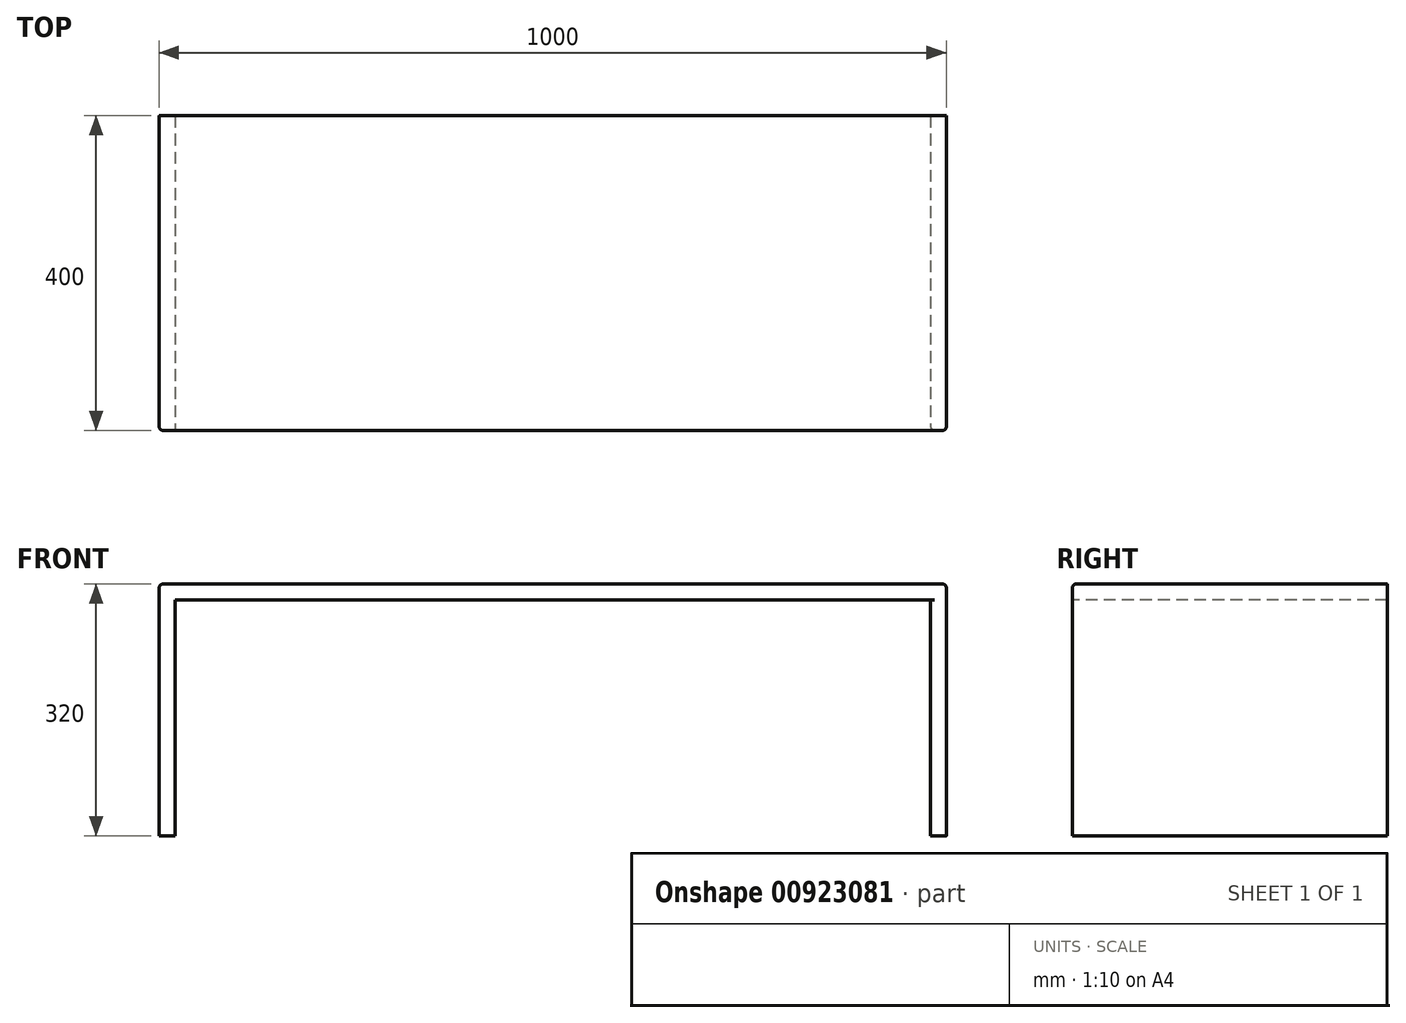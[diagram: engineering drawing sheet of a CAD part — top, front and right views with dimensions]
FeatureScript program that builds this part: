
annotation { "Feature Type Name" : "Feature", "Feature Type Description" : "" }
export const myFeature = defineFeature(function(context is Context, id is Id, definition is map)
    precondition{}
    {
        {
            var Q0;
            Q0=qCreatedBy(makeId("Top.planeOp"),FACE);
            var sketch = newSketch(context, id + "F0", { "sketchPlane" : qUnion([Q0])});
            skLineSegment(sketch, "E0.bottom", {"start": v(-578.88, 126.54) * mm, "end": v(421.12, 126.54) * mm});
            skLineSegment(sketch, "E0.top", {"start": v(-578.88, -273.46) * mm, "end": v(421.12, -273.46) * mm});
            skLineSegment(sketch, "E0.left", {"start": v(-578.88, 126.54) * mm, "end": v(-578.88, -273.46) * mm});
            skLineSegment(sketch, "E0.right", {"start": v(421.12, 126.54) * mm, "end": v(421.12, -273.46) * mm});
            skSolve(sketch);
        }
        {
            var Q0;
            Q0=makeQuery(id+"F0.imprint","IMPRINT",FACE,{"disambiguationData":[TD([[makeQuery(id+"F0.imprint","IMPRINT",EDGE,{"derivedFrom":sQuery(id+"F0.wireOp",EDGE,"E0.bottom")}),-1.0]])]});
            extrude(context, id + "F1", {"entities" : qUnion([Q0]), "depth" : 20 * mm, "offsetDistance" : 25 * mm});
        }
        {
            var Q0;
            Q0=makeQuery(id+"F0.imprint","IMPRINT",FACE,{"disambiguationData":[TD([[makeQuery(id+"F0.imprint","IMPRINT",EDGE,{"derivedFrom":sQuery(id+"F0.wireOp",EDGE,"E0.bottom")}),-1.0]])]});
            var sketch = newSketch(context, id + "F2", { "sketchPlane" : qUnion([Q0])});
            skLineSegment(sketch, "E1.bottom", {"start": v(-578.88, 126.54) * mm, "end": v(-558.88, 126.54) * mm});
            skLineSegment(sketch, "E1.top", {"start": v(-578.88, -273.46) * mm, "end": v(-558.88, -273.46) * mm});
            skLineSegment(sketch, "E1.left", {"start": v(-578.88, 126.54) * mm, "end": v(-578.88, -273.46) * mm});
            skLineSegment(sketch, "E1.right", {"start": v(-558.88, 126.54) * mm, "end": v(-558.88, -273.46) * mm});
            skLineSegment(sketch, "E2.bottom", {"start": v(421.12, 126.54) * mm, "end": v(401.12, 126.54) * mm});
            skLineSegment(sketch, "E2.top", {"start": v(421.12, -273.46) * mm, "end": v(401.12, -273.46) * mm});
            skLineSegment(sketch, "E2.left", {"start": v(421.12, 126.54) * mm, "end": v(421.12, -273.46) * mm});
            skLineSegment(sketch, "E2.right", {"start": v(401.12, 126.54) * mm, "end": v(401.12, -273.46) * mm});
            skSolve(sketch);
        }
        {
            var Q0;
            Q0 = qSketchRegion(id + "F2", true);
            extrude(context, id + "F3", {"entities" : qUnion([Q0]), "operationType" : NewBodyOperationType.ADD, "oppositeDirection" : true, "depth" : 300 * mm, "offsetDistance" : 25 * mm});
        }
        {
            var Q0;
            Q0=makeQuery(id+"F1.opExtrude","CAP_EDGE",EDGE,{"disambiguationData":[OSD([sQuery(id+"F0.wireOp",EDGE,"E0.top")])],"isStart":false});
            fillet(context, id + "F4", {"entities" : qUnion([Q0]), "radius" : 5 * mm, "tangentPropagation" : true, "allowEdgeOverflow" : false});
        }
        {
            var Q0;
            Q0=makeQuery(id+"F1.opExtrude","CAP_EDGE",EDGE,{"disambiguationData":[OSD([sQuery(id+"F0.wireOp",EDGE,"E0.right")])],"isStart":false});
            fillet(context, id + "F5", {"entities" : qUnion([Q0]), "radius" : 5 * mm, "tangentPropagation" : true, "allowEdgeOverflow" : false});
        }
        {
            var Q0;
            Q0=makeQuery(id+"F3.opExtrude","SWEPT_EDGE",EDGE,{"disambiguationData":[OSD([sQuery(id+"F0.wireOp",EDGE,"E0.top"),sQuery(id+"F2.wireOp",EDGE,"E2.top"),sQuery(id+"F2.wireOp",EDGE,"E2.right")])]});
            var Q1;
            Q1=makeQuery(id+"F1.opExtrude","CAP_EDGE",EDGE,{"disambiguationData":[OSD([sQuery(id+"F0.wireOp",EDGE,"E0.left")])],"isStart":false});
            fillet(context, id + "F6", {"entities" : qUnion([Q0, Q1]), "radius" : 5 * mm, "tangentPropagation" : true, "allowEdgeOverflow" : false});
        }
    });
